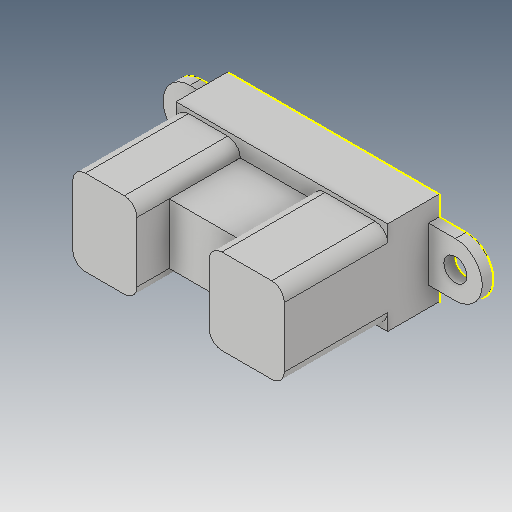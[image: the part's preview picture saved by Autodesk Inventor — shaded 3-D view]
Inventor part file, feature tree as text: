
AUTODESK INVENTOR PART (.ipt)
format: ipt  version: 2018.3 (Build 223284000, 284)  size: 251,392 bytes
history: native  units: in
note: dims shown in document units (in); Inventor stores cm internally (conversion verified against a paired STEP export)
features: sketch x10, extrude x9, fillet x1, plane x1
ambient origin geometry x8: Origin, YZ Plane, XZ Plane, XY Plane, X Axis, Y Axis, Z Axis, Center Point
bodies: Solid1 (feature_tree)
feature tree (21):
  extrude  "Extrusion1"  Depth=0.8504in TaperAngle=0.0deg
  extrude  "Extrusion2"  Depth=0.3976in
  extrude  "Extrusion3"  Depth=0.5669in TaperAngle=0.0deg
  extrude  "Extrusion4"  Depth=0.4114in
  fillet  "Fillet1"  Radius=0.4685in
  extrude  "Extrusion5"  Depth=0.0215in
  extrude  "Extrusion6"  Depth=0.5669in TaperAngle=0.0deg
  extrude  "Extrusion7"  Depth=0.3307in
  plane  "Work Plane5"
  extrude  "Extrusion8"  Depth=0.3898in TaperAngle=0.0deg
  extrude  "Extrusion9"  Depth=0.3815in
  sketch  "Sketch13"  dims[d41=0.2953in d42=0.126in d43=0.2953in d44=0.126in d46=1.1614in d47=0.0591in d48=0.0in d51=0.2362in d52=0.0in d53=-0.1299in d54=0.0472in d55=0.0in d56=0.0472in d57=0.0in]
  sketch  "Sketch1"  dims[d1=0.7441in d2=0.8504in d3=0.0in]
  sketch  "Sketch2"  dims[d6=0.5118in d11=0.3976in]
  sketch  "Sketch4"  dims[d16=0.8504in d17=0.0in d20=0.5669in d21=0.0in]
  sketch  "Sketch5"  dims[d22=0.3524in d23=0.4114in d24=0.4685in]
  sketch  "Sketch6"  dims[d25=0.4685in d26=0.0215in]
  sketch  "Sketch8"  dims[d27=0.0215in d28=0.5669in d29=0.0in]
  sketch  "Sketch10"  dims[d30=0.0689in d31=0.3307in]
  sketch  "Sketch11"  dims[d32=0.0905in d33=0.3898in d34=0.0in]
  sketch  "Sketch12"  dims[d39=0.3815in d40=1.4567in]
